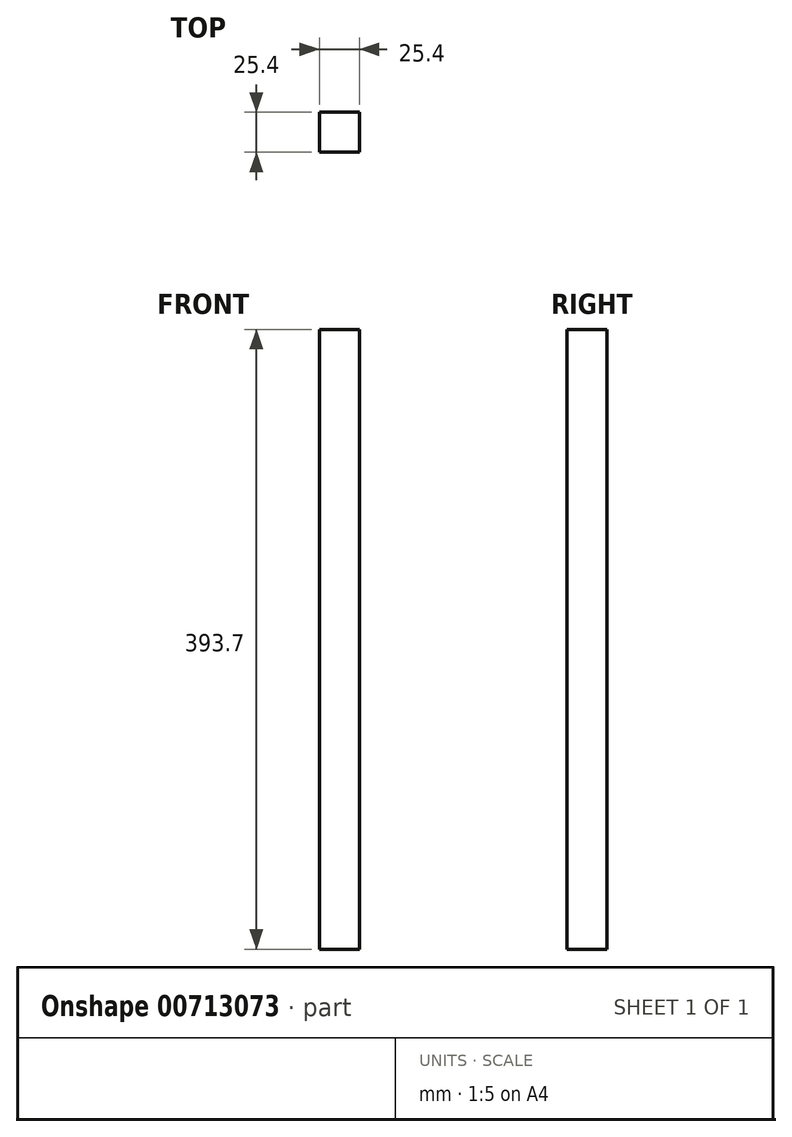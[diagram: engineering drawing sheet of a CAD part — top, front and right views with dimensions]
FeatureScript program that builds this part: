
annotation { "Feature Type Name" : "Feature", "Feature Type Description" : "" }
export const myFeature = defineFeature(function(context is Context, id is Id, definition is map)
    precondition{}
    {
        {
            var Q0;
            Q0=qCreatedBy(makeId("Top.planeOp"),FACE);
            var sketch = newSketch(context, id + "F0", { "sketchPlane" : qUnion([Q0])});
            skLineSegment(sketch, "E0.bottom", {"start": v(-123.54, 61.08) * mm, "end": v(-98.14, 61.08) * mm});
            skLineSegment(sketch, "E0.top", {"start": v(-123.54, 35.68) * mm, "end": v(-98.14, 35.68) * mm});
            skLineSegment(sketch, "E0.left", {"start": v(-123.54, 61.08) * mm, "end": v(-123.54, 35.68) * mm});
            skLineSegment(sketch, "E0.right", {"start": v(-98.14, 61.08) * mm, "end": v(-98.14, 35.68) * mm});
            skSolve(sketch);
        }
        {
            var Q0;
            Q0=makeQuery(id+"F0.imprint","IMPRINT",FACE,{"disambiguationData":[TD([[makeQuery(id+"F0.imprint","IMPRINT",EDGE,{"derivedFrom":sQuery(id+"F0.wireOp",EDGE,"E0.bottom")}),-1.0]])]});
            extrude(context, id + "F1", {"entities" : qUnion([Q0]), "depth" : 393.7 * mm});
        }
    });
